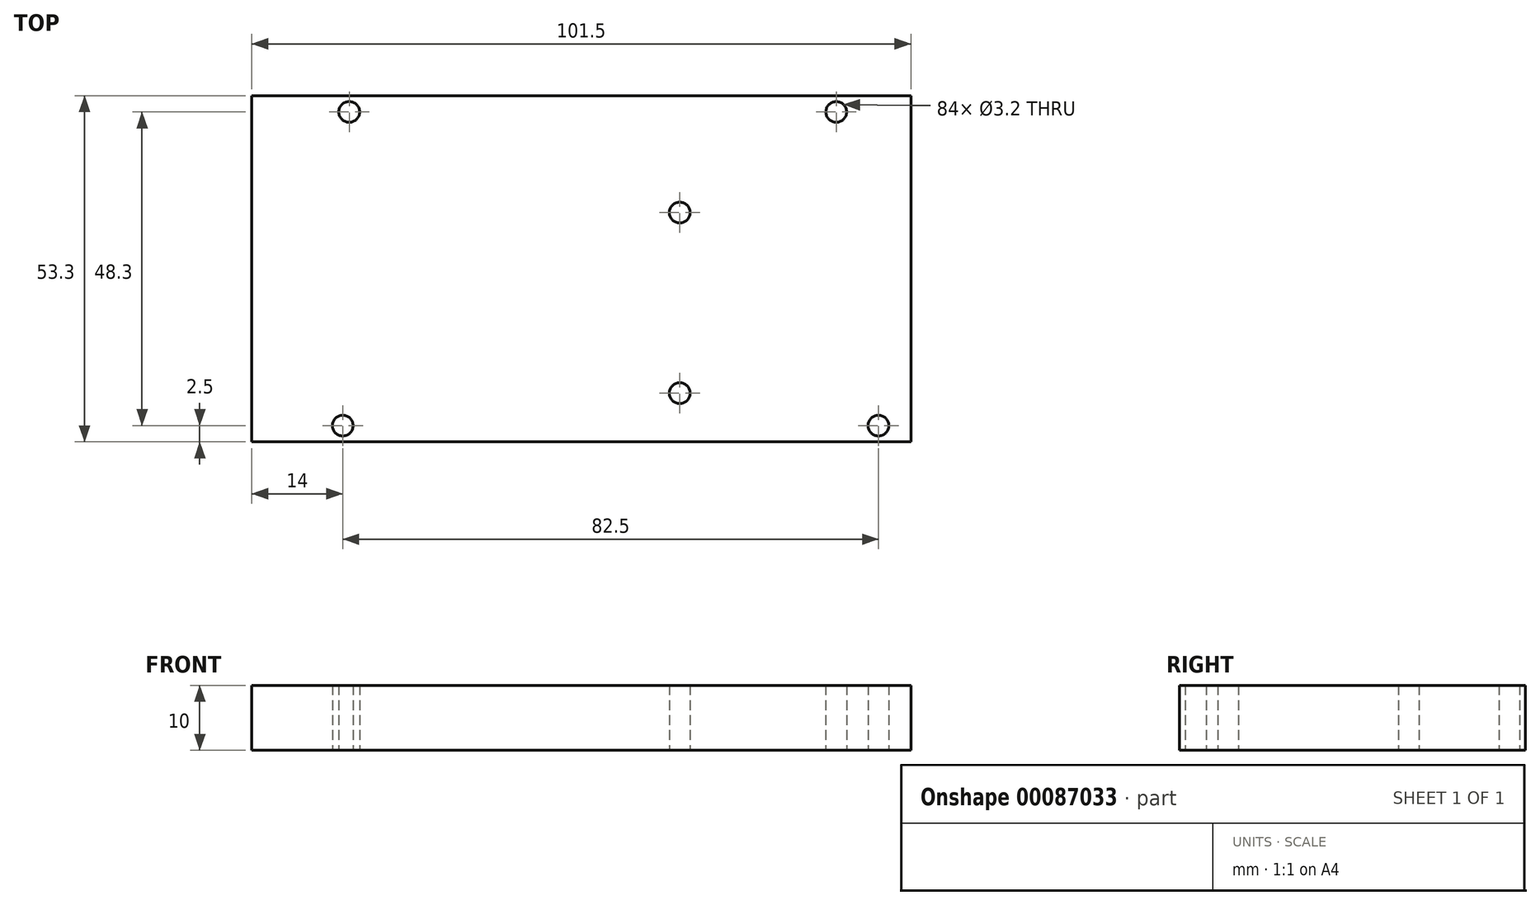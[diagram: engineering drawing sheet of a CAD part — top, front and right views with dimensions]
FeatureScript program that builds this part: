
annotation { "Feature Type Name" : "Feature", "Feature Type Description" : "" }
export const myFeature = defineFeature(function(context is Context, id is Id, definition is map)
    precondition{}
    {
        {
            var Q0;
            Q0=qCreatedBy(makeId("Top.planeOp"),FACE);
            var sketch = newSketch(context, id + "F0", { "sketchPlane" : qUnion([Q0])});
            skLineSegment(sketch, "E0", {"start": v(-50.75, 26.65) * mm, "end": v(-50.75, -26.65) * mm});
            skLineSegment(sketch, "E1", {"start": v(-50.75, -26.65) * mm, "end": v(50.75, -26.65) * mm});
            skLineSegment(sketch, "E2", {"start": v(50.75, -26.65) * mm, "end": v(50.75, 26.65) * mm});
            skLineSegment(sketch, "E3", {"start": v(50.75, 26.65) * mm, "end": v(-50.75, 26.65) * mm});
            skLineSegment(sketch, "E4", {"start": v(-50.75, 26.65) * mm, "end": v(50.75, -26.65) * mm, "construction": true});
            skLineSegment(sketch, "E5", {"start": v(50.75, 26.65) * mm, "end": v(-50.75, -26.65) * mm, "construction": true});
            skPoint(sketch, "E6", {"position": v(0, 0) * mm});
            skCircle(sketch, "E7", {"center": v(45.75, -24.15) * mm, "radius": 1.6 * mm});
            skCircle(sketch, "E8", {"center": v(39.25, 24.15) * mm, "radius": 1.6 * mm});
            skCircle(sketch, "E9", {"center": v(-35.75, 24.15) * mm, "radius": 1.6 * mm});
            skCircle(sketch, "E10", {"center": v(-36.75, -24.15) * mm, "radius": 1.6 * mm});
            skLineSegment(sketch, "E11", {"start": v(-36.75, -24.15) * mm, "end": v(45.75, -24.15) * mm, "construction": true});
            skLineSegment(sketch, "E12", {"start": v(-35.75, 24.15) * mm, "end": v(39.25, 24.15) * mm, "construction": true});
            skCircle(sketch, "E13", {"center": v(15.15, 8.65) * mm, "radius": 1.6 * mm});
            skCircle(sketch, "E14", {"center": v(15.15, -19.15) * mm, "radius": 1.6 * mm});
            skLineSegment(sketch, "E15", {"start": v(15.15, 8.65) * mm, "end": v(15.15, -19.15) * mm, "construction": true});
            skSolve(sketch);
        }
        {
            var Q0;
            Q0=makeQuery(id+"F0.imprint","IMPRINT",FACE,{"disambiguationData":[TD([[makeQuery(id+"F0.imprint","IMPRINT",EDGE,{"derivedFrom":sQuery(id+"F0.wireOp",EDGE,"E0")}),1.0]])]});
            extrude(context, id + "F1", {"entities" : qUnion([Q0]), "depth" : 10 * mm});
        }
    });
